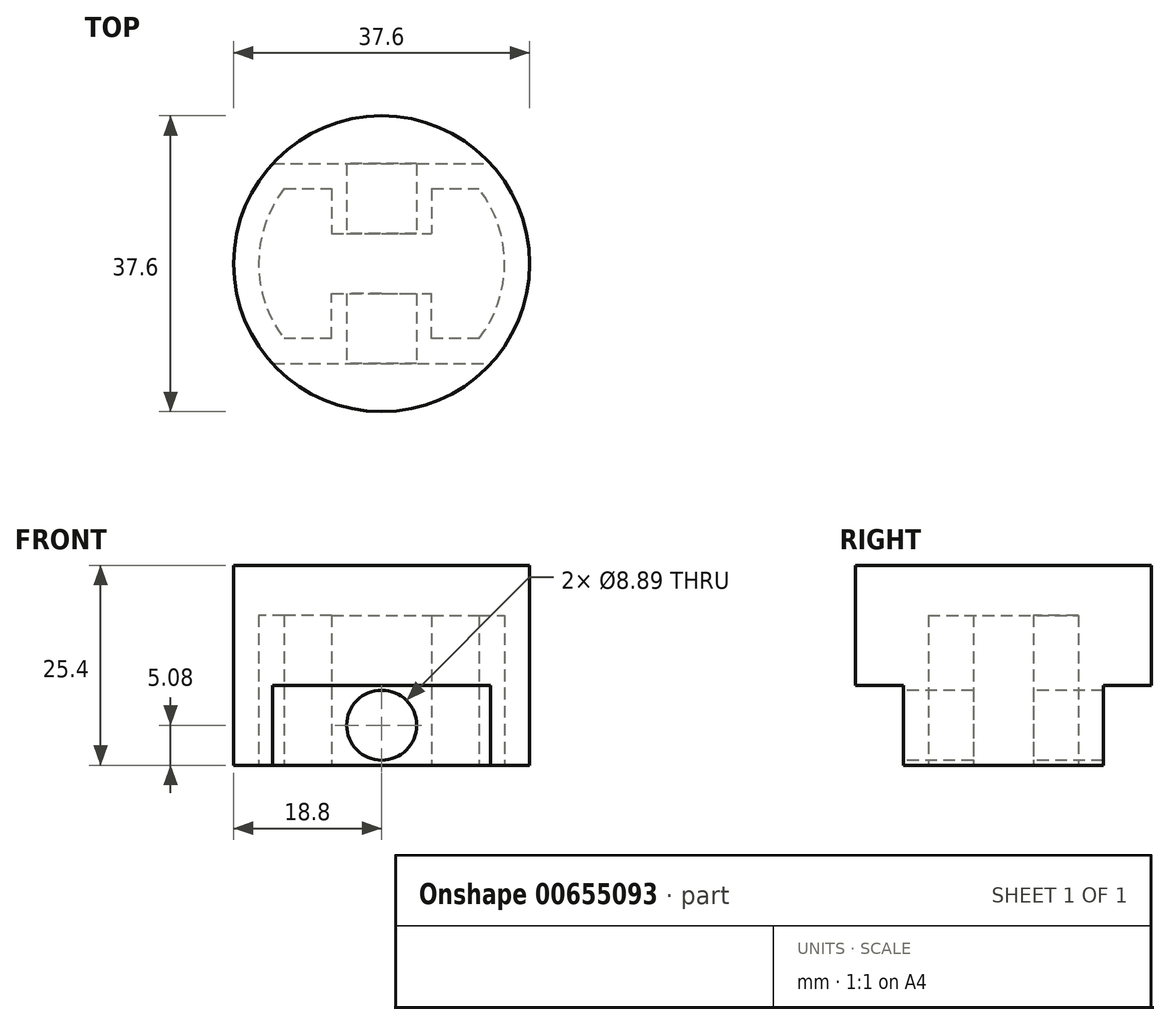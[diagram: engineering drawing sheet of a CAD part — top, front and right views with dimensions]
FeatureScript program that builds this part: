
annotation { "Feature Type Name" : "Feature", "Feature Type Description" : "" }
export const myFeature = defineFeature(function(context is Context, id is Id, definition is map)
    precondition{}
    {
        {
            var Q0;
            Q0=qCreatedBy(makeId("Top.planeOp"),FACE);
            var sketch = newSketch(context, id + "F0", { "sketchPlane" : qUnion([Q0])});
            skCircle(sketch, "E0", {"center": v(0, 0) * mm, "radius": 18.8 * mm});
            skSolve(sketch);
        }
        {
            var Q0;
            Q0 = qSketchRegion(id + "F0", true);
            extrude(context, id + "F1", {"entities" : qUnion([Q0]), "oppositeDirection" : true, "depth" : 25.4 * mm, "offsetDistance" : 25.4 * mm});
        }
        {
            var Q0;
            Q0=makeQuery(id+"F1.opExtrude","CAP_FACE",FACE,{"disambiguationData":[OSD([sQuery(id+"F0.wireOp",EDGE,"E0")])],"isStart":false});
            var sketch = newSketch(context, id + "F2", { "sketchPlane" : qUnion([Q0])});
            skArc(sketch, "E1", {"start": v(-13.86, -12.7) * mm, "mid": v(0, -18.8) * mm, "end": v(13.86, -12.7) * mm});
            skArc(sketch, "E2.trimOffspring", {"start": v(13.86, 12.7) * mm, "mid": v(0, 18.8) * mm, "end": v(-13.86, 12.7) * mm});
            skLineSegment(sketch, "E3", {"start": v(-13.86, 12.7) * mm, "end": v(13.86, 12.7) * mm});
            skLineSegment(sketch, "E4", {"start": v(-13.86, -12.7) * mm, "end": v(13.86, -12.7) * mm});
            skSolve(sketch);
        }
        {
            var Q0;
            Q0 = qSketchRegion(id + "F2", true);
            extrude(context, id + "F3", {"entities" : qUnion([Q0]), "operationType" : NewBodyOperationType.REMOVE, "oppositeDirection" : true, "depth" : 10.16 * mm, "offsetDistance" : 25.4 * mm});
        }
        {
            var Q0;
            Q0=makeQuery(id+"F1.opExtrude","CAP_FACE",FACE,{"disambiguationData":[OSD([sQuery(id+"F0.wireOp",EDGE,"E0")])],"isStart":false});
            var sketch = newSketch(context, id + "F4", { "sketchPlane" : qUnion([Q0])});
            skArc(sketch, "E5.0", {"start": v(-12.38, 9.52) * mm, "mid": v(-15.62, 0) * mm, "end": v(-12.38, -9.52) * mm});
            skLineSegment(sketch, "E5.1", {"start": v(12.38, 9.52) * mm, "end": v(6.35, 9.52) * mm});
            skArc(sketch, "E5.2", {"start": v(12.38, -9.52) * mm, "mid": v(15.62, 0) * mm, "end": v(12.38, 9.52) * mm});
            skLineSegment(sketch, "E5.3", {"start": v(-12.38, -9.52) * mm, "end": v(-6.35, -9.52) * mm});
            skLineSegment(sketch, "E6.top", {"start": v(-6.35, 3.81) * mm, "end": v(6.35, 3.81) * mm});
            skLineSegment(sketch, "E6.left", {"start": v(-6.35, 9.52) * mm, "end": v(-6.35, 3.8) * mm});
            skLineSegment(sketch, "E6.right", {"start": v(6.35, 9.53) * mm, "end": v(6.35, 3.81) * mm});
            skLineSegment(sketch, "E7.top", {"start": v(-6.35, -3.81) * mm, "end": v(6.35, -3.81) * mm});
            skLineSegment(sketch, "E7.left", {"start": v(-6.35, -9.52) * mm, "end": v(-6.35, -3.81) * mm});
            skLineSegment(sketch, "E7.right", {"start": v(6.35, -9.52) * mm, "end": v(6.35, -3.81) * mm});
            skLineSegment(sketch, "E8.trimOffspring", {"start": v(-6.35, 9.52) * mm, "end": v(-12.38, 9.52) * mm});
            skLineSegment(sketch, "E9.trimOffspring", {"start": v(6.35, -9.52) * mm, "end": v(12.38, -9.52) * mm});
            skSolve(sketch);
        }
        {
            var Q0;
            Q0 = qSketchRegion(id + "F4", true);
            extrude(context, id + "F5", {"entities" : qUnion([Q0]), "operationType" : NewBodyOperationType.REMOVE, "oppositeDirection" : true, "depth" : 19.05 * mm, "offsetDistance" : 25.4 * mm});
        }
        {
            var Q0;
            Q0=makeQuery(id+"F3.boolean.opBoolean","COPY",FACE,{"derivedFrom":makeQuery(id+"F3.opExtrude","SWEPT_FACE",FACE,{"disambiguationData":[OSD([sQuery(id+"F2.wireOp",EDGE,"E3")])]})});
            var sketch = newSketch(context, id + "F6", { "sketchPlane" : qUnion([Q0])});
            skCircle(sketch, "E10", {"center": v(0, -20.32) * mm, "radius": 4.45 * mm});
            skSolve(sketch);
        }
        {
            var Q0;
            Q0 = qSketchRegion(id + "F6", true);
            extrude(context, id + "F7", {"entities" : qUnion([Q0]), "operationType" : NewBodyOperationType.REMOVE, "endBound" : BoundingType.THROUGH_ALL, "oppositeDirection" : true, "depth" : 25.4 * mm, "offsetDistance" : 25.4 * mm});
        }
    });
